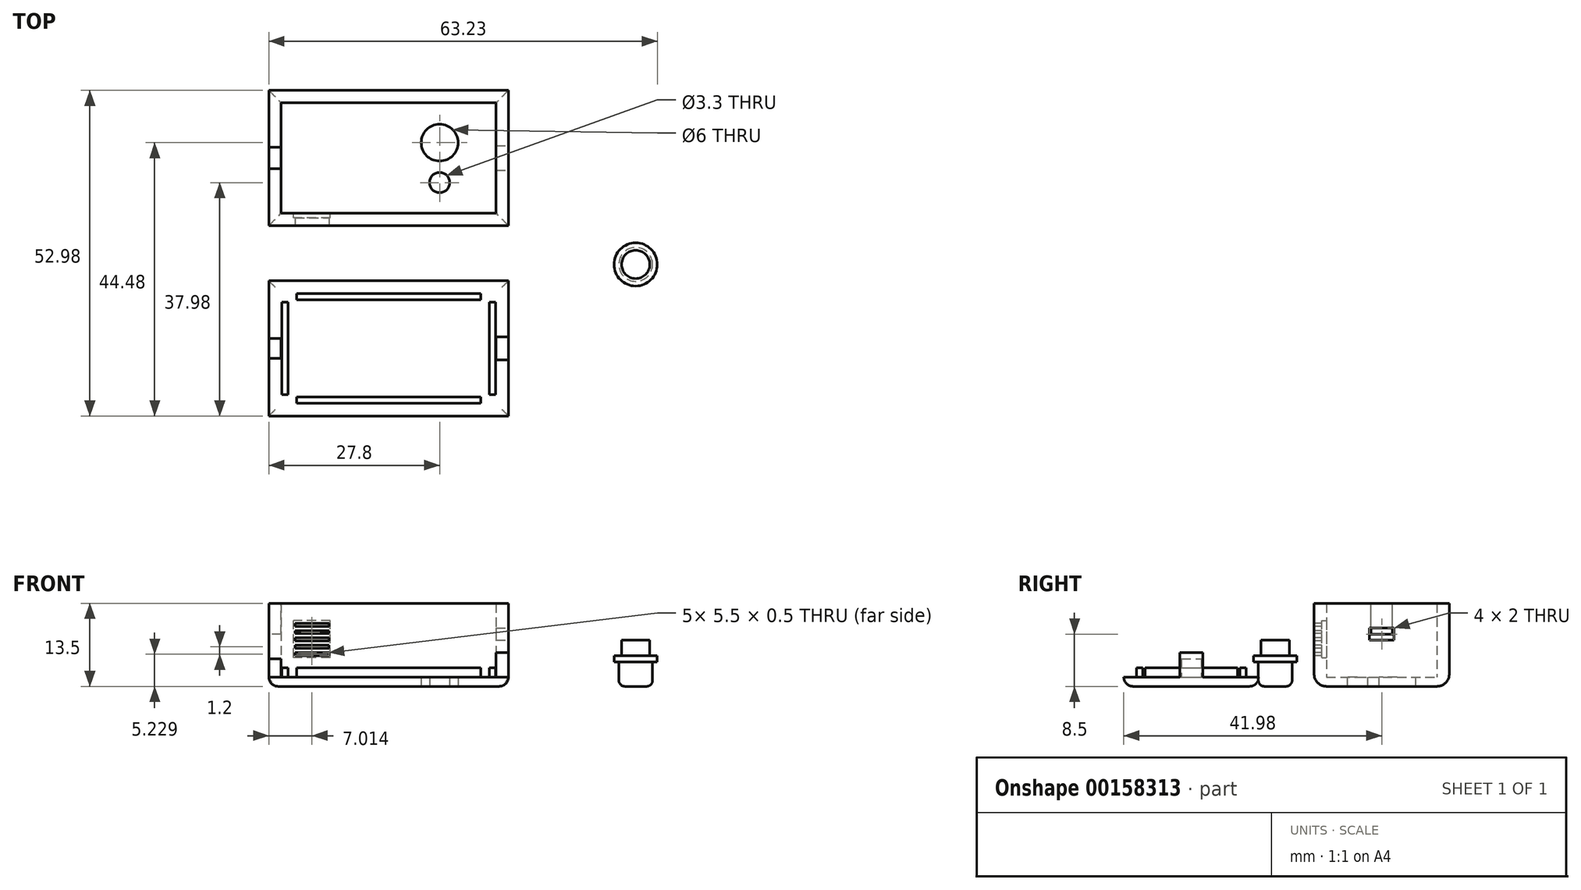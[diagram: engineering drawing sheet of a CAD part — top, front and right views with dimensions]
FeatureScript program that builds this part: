
annotation { "Feature Type Name" : "Feature", "Feature Type Description" : "" }
export const myFeature = defineFeature(function(context is Context, id is Id, definition is map)
    precondition{}
    {
        {
            var Q0;
            Q0=qCreatedBy(makeId("Top.planeOp"),FACE);
            var sketch = newSketch(context, id + "F0", { "sketchPlane" : qUnion([Q0])});
            skLineSegment(sketch, "E0.bottom", {"start": v(17.5, -9) * mm, "end": v(-17.5, -9) * mm});
            skLineSegment(sketch, "E0.top", {"start": v(17.5, 9) * mm, "end": v(-17.5, 9) * mm});
            skLineSegment(sketch, "E0.left", {"start": v(17.5, -9) * mm, "end": v(17.5, 9) * mm});
            skLineSegment(sketch, "E0.right", {"start": v(-17.5, -9) * mm, "end": v(-17.5, 9) * mm});
            skPoint(sketch, "E0.middle", {"position": v(0, 0) * mm});
            skLineSegment(sketch, "E1.0", {"start": v(19.5, 11) * mm, "end": v(-19.5, 11) * mm});
            skLineSegment(sketch, "E1.1", {"start": v(19.5, -11) * mm, "end": v(19.5, 11) * mm});
            skLineSegment(sketch, "E1.2", {"start": v(19.5, -11) * mm, "end": v(-19.5, -11) * mm});
            skLineSegment(sketch, "E1.3", {"start": v(-19.5, -11) * mm, "end": v(-19.5, 11) * mm});
            skPoint(sketch, "E2", {"position": v(8.3, -4) * mm});
            skPoint(sketch, "E3", {"position": v(8.3, 2.5) * mm});
            skSolve(sketch);
        }
        {
            var Q0;
            Q0=makeQuery(id+"F0.imprint","IMPRINT",FACE,{"disambiguationData":[TD([[makeQuery(id+"F0.imprint","IMPRINT",EDGE,{"derivedFrom":sQuery(id+"F0.wireOp",EDGE,"E0.bottom")}),-1.0]])]});
            extrude(context, id + "F1", {"entities" : qUnion([Q0]), "depth" : 1.5 * mm});
        }
        {
            var Q0;
            Q0=makeQuery(id+"F0.imprint","IMPRINT",FACE,{"disambiguationData":[TD([[makeQuery(id+"F0.imprint","IMPRINT",EDGE,{"derivedFrom":sQuery(id+"F0.wireOp",EDGE,"E0.bottom")}),1.0]])]});
            extrude(context, id + "F2", {"entities" : qUnion([Q0]), "operationType" : NewBodyOperationType.ADD, "depth" : 13.5 * mm});
        }
        {
            var Q0;
            Q0=sQuery(id+"F0.wireOp",VERTEX,"E2");
            var Q1;
            Q1=makeQuery(id+"F1.opExtrude","SWEPT_BODY",BODY,{"disambiguationData":[OSD([sQuery(id+"F0.wireOp",EDGE,"E0.bottom"),sQuery(id+"F0.wireOp",EDGE,"E0.top"),sQuery(id+"F0.wireOp",EDGE,"E0.left"),sQuery(id+"F0.wireOp",EDGE,"E0.right")])]});
            hole(context, id + "F3", {"style" : HoleStyle.SIMPLE, "endStyle" : HoleEndStyle.BLIND, "oppositeDirection" : true, "holeDiameter" : 3.3 * mm, "holeDepth" : 5 * mm, "locations" : qUnion([Q0]), "scope" : qUnion([Q1])});
        }
        {
            var Q0;
            Q0=makeQuery(id+"F2.opExtrude","SWEPT_FACE",FACE,{"disambiguationData":[OSD([sQuery(id+"F0.wireOp",EDGE,"E1.2")])]});
            cPlane(context, id + "F4", {"entities" : qUnion([Q0]), "cplaneType" : CPlaneType.OFFSET, "offset" : 2 * mm, "oppositeDirection" : true, "width" : 150 * mm, "height" : 150 * mm});
        }
        {
            var Q0;
            Q0=sQuery(id+"F0.wireOp",VERTEX,"E3");
            var Q1;
            Q1=makeQuery(id+"F1.opExtrude","SWEPT_BODY",BODY,{"disambiguationData":[OSD([sQuery(id+"F0.wireOp",EDGE,"E0.bottom"),sQuery(id+"F0.wireOp",EDGE,"E0.top"),sQuery(id+"F0.wireOp",EDGE,"E0.left"),sQuery(id+"F0.wireOp",EDGE,"E0.right")])]});
            hole(context, id + "F5", {"style" : HoleStyle.SIMPLE, "endStyle" : HoleEndStyle.BLIND, "oppositeDirection" : true, "holeDiameter" : 6 * mm, "holeDepth" : 5 * mm, "locations" : qUnion([Q0]), "scope" : qUnion([Q1])});
        }
        {
            var Q0;
            Q0=makeQuery(id+"F2.opExtrude","SWEPT_FACE",FACE,{"disambiguationData":[OSD([sQuery(id+"F0.wireOp",EDGE,"E1.1")])]});
            var sketch = newSketch(context, id + "F6", { "sketchPlane" : qUnion([Q0])});
            skPoint(sketch, "E4", {"position": v(0, 8.5) * mm});
            skPoint(sketch, "E4.positionSnap0", {"position": v(0, 13.5) * mm});
            skLineSegment(sketch, "E5.bottom", {"start": v(2, 7.5) * mm, "end": v(-2, 7.5) * mm});
            skLineSegment(sketch, "E5.top", {"start": v(2, 9.5) * mm, "end": v(-2, 9.5) * mm});
            skLineSegment(sketch, "E5.left", {"start": v(2, 7.5) * mm, "end": v(2, 9.5) * mm});
            skLineSegment(sketch, "E5.right", {"start": v(-2, 7.5) * mm, "end": v(-2, 9.5) * mm});
            skLineSegment(sketch, "E6.bottom", {"start": v(-2, 9.5) * mm, "end": v(2, 9.5) * mm});
            skLineSegment(sketch, "E6.top", {"start": v(-2, 9.5) * mm, "end": v(2, 9.5) * mm});
            skLineSegment(sketch, "E6.left", {"start": v(-2, 9.5) * mm, "end": v(-2, 9.5) * mm});
            skLineSegment(sketch, "E6.right", {"start": v(2, 9.5) * mm, "end": v(2, 9.5) * mm});
            skLineSegment(sketch, "E7.top", {"start": v(-2, 13.5) * mm, "end": v(2, 13.5) * mm});
            skLineSegment(sketch, "E7.left", {"start": v(-2, 9.5) * mm, "end": v(-2, 13.5) * mm});
            skLineSegment(sketch, "E7.right", {"start": v(2, 9.5) * mm, "end": v(2, 13.5) * mm});
            skSolve(sketch);
        }
        {
            var Q0;
            Q0=qCreatedBy(makeId("Top.planeOp"),FACE);
            var sketch = newSketch(context, id + "F7", { "sketchPlane" : qUnion([Q0])});
            skCircle(sketch, "E8", {"center": v(40.21, -17.32) * mm, "radius": 2.75 * mm});
            skCircle(sketch, "E9", {"center": v(40.21, -17.32) * mm, "radius": 2.3 * mm});
            skSolve(sketch);
        }
        {
            var Q0;
            Q0=makeQuery(id+"F7.imprint","IMPRINT",FACE,{"disambiguationData":[TD([[makeQuery(id+"F7.imprint","IMPRINT",EDGE,{"derivedFrom":sQuery(id+"F7.wireOp",EDGE,"E9")}),1.0]])]});
            extrude(context, id + "F8", {"entities" : qUnion([Q0]), "depth" : 7.5 * mm});
        }
        {
            var Q0;
            Q0=makeQuery(id+"F7.imprint","IMPRINT",FACE,{"disambiguationData":[TD([[makeQuery(id+"F7.imprint","IMPRINT",EDGE,{"derivedFrom":sQuery(id+"F7.wireOp",EDGE,"E8")}),1.0]])]});
            extrude(context, id + "F9", {"entities" : qUnion([Q0]), "operationType" : NewBodyOperationType.ADD, "depth" : 4 * mm});
        }
        {
            var Q0;
            {var subQ0=sQuery(id+"F7.wireOp",EDGE,"E9");Q0=makeQuery(id+"F9.boolean.opBoolean","MERGE",FACE,{"derivedFrom":[makeQuery(id+"F8.opExtrude","CAP_FACE",FACE,{"disambiguationData":[OSD([subQ0])],"isStart":true}),makeQuery(id+"F9.opExtrude","CAP_FACE",FACE,{"disambiguationData":[OSD([sQuery(id+"F7.wireOp",EDGE,"E8"),subQ0])],"isStart":true})]});}
            var Q1;
            Q1=makeQuery(id+"F9.opExtrude","CAP_EDGE",EDGE,{"disambiguationData":[OSD([sQuery(id+"F7.wireOp",EDGE,"E8")])],"isStart":true});
            fillet(context, id + "F10", {"entities" : qUnion([Q0, Q1]), "radius" : 1 * mm, "tangentPropagation" : true, "allowEdgeOverflow" : false});
        }
        {
            var Q0;
            Q0=makeQuery(id+"F9.opExtrude","CAP_FACE",FACE,{"disambiguationData":[OSD([sQuery(id+"F7.wireOp",EDGE,"E8"),sQuery(id+"F7.wireOp",EDGE,"E9")])],"isStart":false});
            var sketch = newSketch(context, id + "F11", { "sketchPlane" : qUnion([Q0])});
            skCircle(sketch, "E10", {"center": v(40.21, -17.32) * mm, "radius": 2.75 * mm});
            skPoint(sketch, "E10.first.point", {"position": v(37.94, -15.78) * mm});
            skPoint(sketch, "E10.second.point", {"position": v(37.8, -16.01) * mm});
            skPoint(sketch, "E10.third.point", {"position": v(37.94, -15.78) * mm});
            skCircle(sketch, "E11", {"center": v(40.21, -17.32) * mm, "radius": 3.51 * mm});
            skSolve(sketch);
        }
        {
            var Q0;
            Q0=makeQuery(id+"F11.imprint","IMPRINT",FACE,{"disambiguationData":[TD([[makeQuery(id+"F11.imprint","IMPRINT",EDGE,{"derivedFrom":sQuery(id+"F11.wireOp",EDGE,"E10")}),-1.0]])]});
            var Q1;
            Q1=makeQuery(id+"F11.imprint","IMPRINT",FACE,{"disambiguationData":[TD([[makeQuery(id+"F11.imprint","IMPRINT",EDGE,{"derivedFrom":sQuery(id+"F11.wireOp",EDGE,"E10")}),1.0]])]});
            extrude(context, id + "F12", {"entities" : qUnion([Q0, Q1]), "operationType" : NewBodyOperationType.ADD, "depth" : 1 * mm});
        }
        {
            var Q0;
            Q0=makeQuery(id+"F2.opExtrude","CAP_FACE",FACE,{"disambiguationData":[OSD([sQuery(id+"F0.wireOp",EDGE,"E0.bottom"),sQuery(id+"F0.wireOp",EDGE,"E0.top"),sQuery(id+"F0.wireOp",EDGE,"E0.left"),sQuery(id+"F0.wireOp",EDGE,"E0.right"),sQuery(id+"F0.wireOp",EDGE,"E1.0"),sQuery(id+"F0.wireOp",EDGE,"E1.1"),sQuery(id+"F0.wireOp",EDGE,"E1.2"),sQuery(id+"F0.wireOp",EDGE,"E1.3")])],"isStart":false});
            var sketch = newSketch(context, id + "F13", { "sketchPlane" : qUnion([Q0])});
            skLineSegment(sketch, "E12.bottom", {"start": v(-19.5, 11) * mm, "end": v(19.5, 11) * mm});
            skLineSegment(sketch, "E12.top", {"start": v(-19.5, -11) * mm, "end": v(19.5, -11) * mm});
            skLineSegment(sketch, "E12.left", {"start": v(-19.5, 11) * mm, "end": v(-19.5, -11) * mm});
            skLineSegment(sketch, "E12.right", {"start": v(19.5, 11) * mm, "end": v(19.5, -11) * mm});
            skSolve(sketch);
        }
        {
            var Q0;
            Q0=qCreatedBy(id+"F4.planeOp",FACE);
            var sketch = newSketch(context, id + "F14", { "sketchPlane" : qUnion([Q0])});
            skPoint(sketch, "E13", {"position": v(-12.5, 7.7) * mm});
            skLineSegment(sketch, "E14.bottom", {"start": v(-9.5, 4.7) * mm, "end": v(-15.5, 4.7) * mm});
            skLineSegment(sketch, "E14.top", {"start": v(-9.5, 10.7) * mm, "end": v(-15.5, 10.7) * mm});
            skLineSegment(sketch, "E14.left", {"start": v(-9.5, 4.7) * mm, "end": v(-9.5, 10.7) * mm});
            skLineSegment(sketch, "E14.right", {"start": v(-15.5, 4.7) * mm, "end": v(-15.5, 10.7) * mm});
            skSolve(sketch);
        }
        {
            var Q0;
            Q0=makeQuery(id+"F14.imprint","IMPRINT",FACE,{"disambiguationData":[TD([[makeQuery(id+"F14.imprint","IMPRINT",EDGE,{"derivedFrom":sQuery(id+"F14.wireOp",EDGE,"E14.bottom")}),-1.0]])]});
            extrude(context, id + "F15", {"entities" : qUnion([Q0]), "operationType" : NewBodyOperationType.REMOVE, "endBound" : BoundingType.SYMMETRIC, "depth" : 1.5 * mm});
        }
        {
            var Q0;
            Q0=makeQuery(id+"F2.opExtrude","SWEPT_FACE",FACE,{"disambiguationData":[OSD([sQuery(id+"F0.wireOp",EDGE,"E1.3")])]});
            var sketch = newSketch(context, id + "F16", { "sketchPlane" : qUnion([Q0])});
            skPoint(sketch, "E15", {"position": v(0, 11) * mm});
            skPoint(sketch, "E15.positionSnap0", {"position": v(0, 13.5) * mm});
            skLineSegment(sketch, "E16.bottom", {"start": v(1.75, 8.5) * mm, "end": v(-1.75, 8.5) * mm});
            skLineSegment(sketch, "E16.top", {"start": v(1.75, 13.5) * mm, "end": v(-1.75, 13.5) * mm});
            skLineSegment(sketch, "E16.left", {"start": v(1.75, 8.5) * mm, "end": v(1.75, 13.5) * mm});
            skLineSegment(sketch, "E16.right", {"start": v(-1.75, 8.5) * mm, "end": v(-1.75, 13.5) * mm});
            skSolve(sketch);
        }
        {
            var Q0;
            Q0=makeQuery(id+"F16.imprint","IMPRINT",FACE,{"disambiguationData":[TD([[makeQuery(id+"F16.imprint","IMPRINT",EDGE,{"derivedFrom":sQuery(id+"F16.wireOp",EDGE,"E16.bottom")}),-1.0]])]});
            extrude(context, id + "F17", {"entities" : qUnion([Q0]), "operationType" : NewBodyOperationType.REMOVE, "oppositeDirection" : true, "depth" : 5 * mm});
        }
        {
            var Q0;
            Q0=qCreatedBy(makeId("Top.planeOp"),FACE);
            var sketch = newSketch(context, id + "F18", { "sketchPlane" : qUnion([Q0])});
            skLineSegment(sketch, "E17.bottom", {"start": v(19.5, -41.98) * mm, "end": v(-19.5, -41.98) * mm});
            skLineSegment(sketch, "E17.top", {"start": v(19.5, -19.98) * mm, "end": v(-19.5, -19.98) * mm});
            skLineSegment(sketch, "E17.left", {"start": v(19.5, -41.98) * mm, "end": v(19.5, -19.98) * mm});
            skLineSegment(sketch, "E17.right", {"start": v(-19.5, -41.98) * mm, "end": v(-19.5, -19.98) * mm});
            skPoint(sketch, "E17.middle", {"position": v(0, -30.98) * mm});
            skLineSegment(sketch, "E18.bottom", {"start": v(15, -39.88) * mm, "end": v(-15, -39.88) * mm});
            skLineSegment(sketch, "E18.top", {"start": v(15, -38.88) * mm, "end": v(-15, -38.88) * mm});
            skLineSegment(sketch, "E18.left", {"start": v(15, -39.88) * mm, "end": v(15, -38.88) * mm});
            skLineSegment(sketch, "E18.right", {"start": v(-15, -39.88) * mm, "end": v(-15, -38.88) * mm});
            skPoint(sketch, "E18.middle", {"position": v(0, -39.38) * mm});
            skPoint(sketch, "E18.middle.positionSnap0", {"position": v(0, -41.98) * mm});
            skPoint(sketch, "E18.centerSnap0", {"position": v(0, -41.98) * mm});
            skLineSegment(sketch, "E19.bottom", {"start": v(15, -23.1) * mm, "end": v(-15, -23.1) * mm});
            skLineSegment(sketch, "E19.top", {"start": v(15, -22.1) * mm, "end": v(-15, -22.1) * mm});
            skLineSegment(sketch, "E19.left", {"start": v(15, -23.1) * mm, "end": v(15, -22.1) * mm});
            skLineSegment(sketch, "E19.right", {"start": v(-15, -23.1) * mm, "end": v(-15, -22.1) * mm});
            skPoint(sketch, "E19.middle", {"position": v(0, -22.6) * mm});
            skLineSegment(sketch, "E20.bottom", {"start": v(-16.4, -38.48) * mm, "end": v(-17.4, -38.48) * mm});
            skLineSegment(sketch, "E20.top", {"start": v(-16.4, -23.48) * mm, "end": v(-17.4, -23.48) * mm});
            skLineSegment(sketch, "E20.left", {"start": v(-16.4, -38.48) * mm, "end": v(-16.4, -23.48) * mm});
            skLineSegment(sketch, "E20.right", {"start": v(-17.4, -38.48) * mm, "end": v(-17.4, -23.48) * mm});
            skPoint(sketch, "E20.middle", {"position": v(-16.9, -30.98) * mm});
            skPoint(sketch, "E20.middle.positionSnap0", {"position": v(-19.5, -30.98) * mm});
            skPoint(sketch, "E20.centerSnap0", {"position": v(-19.5, -30.98) * mm});
            skLineSegment(sketch, "E21.bottom", {"start": v(17.4, -38.48) * mm, "end": v(16.4, -38.48) * mm});
            skLineSegment(sketch, "E21.top", {"start": v(17.4, -23.48) * mm, "end": v(16.4, -23.48) * mm});
            skLineSegment(sketch, "E21.left", {"start": v(17.4, -38.48) * mm, "end": v(17.4, -23.48) * mm});
            skLineSegment(sketch, "E21.right", {"start": v(16.4, -38.48) * mm, "end": v(16.4, -23.48) * mm});
            skPoint(sketch, "E21.middle", {"position": v(16.9, -30.98) * mm});
            skPoint(sketch, "E21.middle.positionSnap0", {"position": v(19.5, -30.98) * mm});
            skPoint(sketch, "E21.centerSnap0", {"position": v(19.5, -30.98) * mm});
            skLineSegment(sketch, "E22.bottom", {"start": v(-17.5, -32.58) * mm, "end": v(-19.5, -32.58) * mm});
            skLineSegment(sketch, "E22.top", {"start": v(-17.5, -29.38) * mm, "end": v(-19.5, -29.38) * mm});
            skLineSegment(sketch, "E22.left", {"start": v(-17.5, -32.58) * mm, "end": v(-17.5, -29.38) * mm});
            skLineSegment(sketch, "E22.right", {"start": v(-19.5, -32.58) * mm, "end": v(-19.5, -29.38) * mm});
            skPoint(sketch, "E22.middle", {"position": v(-18.5, -30.98) * mm});
            skLineSegment(sketch, "E23.bottom", {"start": v(19.5, -32.83) * mm, "end": v(17.5, -32.83) * mm});
            skLineSegment(sketch, "E23.top", {"start": v(19.5, -29.13) * mm, "end": v(17.5, -29.13) * mm});
            skLineSegment(sketch, "E23.left", {"start": v(19.5, -32.83) * mm, "end": v(19.5, -29.13) * mm});
            skLineSegment(sketch, "E23.right", {"start": v(17.5, -32.83) * mm, "end": v(17.5, -29.13) * mm});
            skPoint(sketch, "E23.middle", {"position": v(18.5, -30.98) * mm});
            skSolve(sketch);
        }
        {
            var Q0;
            {var subQ1=sQuery(id+"F18.wireOp",EDGE,"E17.bottom");Q0=makeQuery(id+"F18.imprint","IMPRINT",FACE,{"disambiguationData":[TD([[makeQuery(id+"F18.imprint","IMPRINT",EDGE,{"derivedFrom":subQ1}),-1.0]])]});}
            extrude(context, id + "F19", {"entities" : qUnion([Q0]), "depth" : 1.5 * mm});
        }
        {
            var Q0;
            Q0=makeQuery(id+"F18.imprint","IMPRINT",FACE,{"disambiguationData":[TD([[makeQuery(id+"F18.imprint","IMPRINT",EDGE,{"derivedFrom":sQuery(id+"F18.wireOp",EDGE,"E19.bottom")}),-1.0]])]});
            var Q1;
            Q1=makeQuery(id+"F18.imprint","IMPRINT",FACE,{"disambiguationData":[TD([[makeQuery(id+"F18.imprint","IMPRINT",EDGE,{"derivedFrom":sQuery(id+"F18.wireOp",EDGE,"E20.bottom")}),-1.0]])]});
            var Q2;
            Q2=makeQuery(id+"F18.imprint","IMPRINT",FACE,{"disambiguationData":[TD([[makeQuery(id+"F18.imprint","IMPRINT",EDGE,{"derivedFrom":sQuery(id+"F18.wireOp",EDGE,"E18.bottom")}),-1.0]])]});
            var Q3;
            Q3=makeQuery(id+"F18.imprint","IMPRINT",FACE,{"disambiguationData":[TD([[makeQuery(id+"F18.imprint","IMPRINT",EDGE,{"derivedFrom":sQuery(id+"F18.wireOp",EDGE,"E21.bottom")}),-1.0]])]});
            extrude(context, id + "F20", {"entities" : qUnion([Q0, Q1, Q2, Q3]), "operationType" : NewBodyOperationType.ADD, "depth" : 3 * mm});
        }
        {
            var Q0;
            Q0=makeQuery(id+"F6.imprint","IMPRINT",FACE,{"disambiguationData":[TD([[makeQuery(id+"F6.imprint","IMPRINT",EDGE,{"derivedFrom":sQuery(id+"F6.wireOp",EDGE,"E5.bottom")}),-1.0]])]});
            var Q1;
            Q1=makeQuery(id+"F6.imprint","IMPRINT",FACE,{"disambiguationData":[TD([[makeQuery(id+"F6.imprint","IMPRINT",EDGE,{"derivedFrom":sQuery(id+"F6.wireOp",EDGE,"E6.bottom")}),1.0]])]});
            extrude(context, id + "F21", {"entities" : qUnion([Q0, Q1]), "operationType" : NewBodyOperationType.REMOVE, "oppositeDirection" : true, "depth" : 5 * mm});
        }
        {
            var Q0;
            {var subQ2=sQuery(id+"F18.wireOp",EDGE,"E23.bottom");Q0=makeQuery(id+"F18.imprint","IMPRINT",FACE,{"disambiguationData":[TD([[makeQuery(id+"F18.imprint","IMPRINT",EDGE,{"derivedFrom":subQ2}),-1.0]])]});}
            extrude(context, id + "F22", {"entities" : qUnion([Q0]), "operationType" : NewBodyOperationType.ADD, "depth" : 5.5 * mm});
        }
        {
            var Q0;
            Q0=makeQuery(id+"F2.opExtrude","SWEPT_FACE",FACE,{"disambiguationData":[OSD([sQuery(id+"F0.wireOp",EDGE,"E1.2")])]});
            var sketch = newSketch(context, id + "F23", { "sketchPlane" : qUnion([Q0])});
            skLineSegment(sketch, "E24.bottom", {"start": v(-15.24, 4.98) * mm, "end": v(-15.24, 5.48) * mm});
            skLineSegment(sketch, "E24.top", {"start": v(-9.74, 4.98) * mm, "end": v(-9.74, 5.48) * mm});
            skLineSegment(sketch, "E24.left", {"start": v(-15.24, 4.98) * mm, "end": v(-9.74, 4.98) * mm});
            skLineSegment(sketch, "E24.right", {"start": v(-15.24, 5.48) * mm, "end": v(-9.74, 5.48) * mm});
            skLineSegment(sketch, "E25.1.0.0", {"start": v(-15.24, 6.68) * mm, "end": v(-9.74, 6.68) * mm});
            skLineSegment(sketch, "E25.1.0.1", {"start": v(-15.24, 6.18) * mm, "end": v(-9.74, 6.18) * mm});
            skLineSegment(sketch, "E25.1.0.2", {"start": v(-9.74, 6.18) * mm, "end": v(-9.74, 6.68) * mm});
            skLineSegment(sketch, "E25.1.0.3", {"start": v(-15.24, 6.18) * mm, "end": v(-15.24, 6.68) * mm});
            skLineSegment(sketch, "E25.2.0.0", {"start": v(-15.24, 7.88) * mm, "end": v(-9.74, 7.88) * mm});
            skLineSegment(sketch, "E25.2.0.1", {"start": v(-15.24, 7.38) * mm, "end": v(-9.74, 7.38) * mm});
            skLineSegment(sketch, "E25.2.0.2", {"start": v(-9.74, 7.38) * mm, "end": v(-9.74, 7.88) * mm});
            skLineSegment(sketch, "E25.2.0.3", {"start": v(-15.24, 7.38) * mm, "end": v(-15.24, 7.88) * mm});
            skLineSegment(sketch, "E25.3.0.0", {"start": v(-15.24, 9.08) * mm, "end": v(-9.74, 9.08) * mm});
            skLineSegment(sketch, "E25.3.0.1", {"start": v(-15.24, 8.58) * mm, "end": v(-9.74, 8.58) * mm});
            skLineSegment(sketch, "E25.3.0.2", {"start": v(-9.74, 8.58) * mm, "end": v(-9.74, 9.08) * mm});
            skLineSegment(sketch, "E25.3.0.3", {"start": v(-15.24, 8.58) * mm, "end": v(-15.24, 9.08) * mm});
            skLineSegment(sketch, "E25.4.0.0", {"start": v(-15.24, 10.28) * mm, "end": v(-9.74, 10.28) * mm});
            skLineSegment(sketch, "E25.4.0.1", {"start": v(-15.24, 9.78) * mm, "end": v(-9.74, 9.78) * mm});
            skLineSegment(sketch, "E25.4.0.2", {"start": v(-9.74, 9.78) * mm, "end": v(-9.74, 10.28) * mm});
            skLineSegment(sketch, "E25.4.0.3", {"start": v(-15.24, 9.78) * mm, "end": v(-15.24, 10.28) * mm});
            skLineSegment(sketch, "E25.direction1", {"start": v(-9.74, 4.98) * mm, "end": v(-9.74, 6.18) * mm, "construction": true});
            skSolve(sketch);
        }
        {
            var Q0;
            Q0=makeQuery(id+"F23.imprint","IMPRINT",FACE,{"disambiguationData":[TD([[makeQuery(id+"F23.imprint","IMPRINT",EDGE,{"derivedFrom":sQuery(id+"F23.wireOp",EDGE,"E24.bottom")}),-1.0]])]});
            var Q1;
            Q1=makeQuery(id+"F23.imprint","IMPRINT",FACE,{"disambiguationData":[TD([[makeQuery(id+"F23.imprint","IMPRINT",EDGE,{"derivedFrom":sQuery(id+"F23.wireOp",EDGE,"E25.1.0.0")}),-1.0]])]});
            var Q2;
            Q2=makeQuery(id+"F23.imprint","IMPRINT",FACE,{"disambiguationData":[TD([[makeQuery(id+"F23.imprint","IMPRINT",EDGE,{"derivedFrom":sQuery(id+"F23.wireOp",EDGE,"E25.2.0.0")}),-1.0]])]});
            var Q3;
            Q3=makeQuery(id+"F23.imprint","IMPRINT",FACE,{"disambiguationData":[TD([[makeQuery(id+"F23.imprint","IMPRINT",EDGE,{"derivedFrom":sQuery(id+"F23.wireOp",EDGE,"E25.3.0.0")}),-1.0]])]});
            var Q4;
            Q4=makeQuery(id+"F23.imprint","IMPRINT",FACE,{"disambiguationData":[TD([[makeQuery(id+"F23.imprint","IMPRINT",EDGE,{"derivedFrom":sQuery(id+"F23.wireOp",EDGE,"E25.4.0.0")}),-1.0]])]});
            var Q5;
            Q5=makeQuery(id+"F23.imprint","IMPRINT",FACE,{"disambiguationData":[TD([[makeQuery(id+"F23.imprint","IMPRINT",EDGE,{"derivedFrom":sQuery(id+"F23.wireOp",EDGE,"61a891a3-ae5f-4639-807f-27233e564d6f.0.5.0")}),-1.0]])]});
            extrude(context, id + "F24", {"entities" : qUnion([Q0, Q1, Q2, Q3, Q4, Q5]), "operationType" : NewBodyOperationType.REMOVE, "oppositeDirection" : true, "depth" : 5 * mm});
        }
        {
            var Q0;
            {var subQ2=sQuery(id+"F18.wireOp",EDGE,"E22.bottom");Q0=makeQuery(id+"F18.imprint","IMPRINT",FACE,{"disambiguationData":[TD([[makeQuery(id+"F18.imprint","IMPRINT",EDGE,{"derivedFrom":subQ2}),-1.0]])]});}
            extrude(context, id + "F25", {"entities" : qUnion([Q0]), "operationType" : NewBodyOperationType.ADD, "depth" : 4.5 * mm});
        }
        {
            var Q0;
            Q0=makeQuery(id+"F2.opExtrude","CAP_EDGE",EDGE,{"disambiguationData":[OSD([sQuery(id+"F0.wireOp",EDGE,"E1.2")])],"isStart":true});
            var Q1;
            Q1=makeQuery(id+"F2.opExtrude","CAP_EDGE",EDGE,{"disambiguationData":[OSD([sQuery(id+"F0.wireOp",EDGE,"E1.3")])],"isStart":true});
            var Q2;
            Q2=makeQuery(id+"F2.opExtrude","CAP_EDGE",EDGE,{"disambiguationData":[OSD([sQuery(id+"F0.wireOp",EDGE,"E1.1")])],"isStart":true});
            var Q3;
            Q3=makeQuery(id+"F2.opExtrude","CAP_EDGE",EDGE,{"disambiguationData":[OSD([sQuery(id+"F0.wireOp",EDGE,"E1.0")])],"isStart":true});
            fillet(context, id + "F26", {"entities" : qUnion([Q0, Q1, Q2, Q3]), "radius" : 2 * mm, "tangentPropagation" : true, "allowEdgeOverflow" : false});
        }
        {
            var Q0;
            {var subQ0=sQuery(id+"F18.wireOp",EDGE,"E22.left");var subQ1=sQuery(id+"F18.wireOp",EDGE,"E22.top");var subQ2=sQuery(id+"F18.wireOp",EDGE,"E22.bottom");var subQ3=sQuery(id+"F18.wireOp",EDGE,"E17.right");var subQ4=sQuery(id+"F18.wireOp",EDGE,"E23.right");var subQ5=sQuery(id+"F18.wireOp",EDGE,"E23.top");var subQ6=sQuery(id+"F18.wireOp",EDGE,"E23.bottom");var subQ7=sQuery(id+"F18.wireOp",EDGE,"E17.left");var subQ8=sQuery(id+"F18.wireOp",EDGE,"E21.right");var subQ9=sQuery(id+"F18.wireOp",EDGE,"E21.left");var subQ10=sQuery(id+"F18.wireOp",EDGE,"E21.top");var subQ11=sQuery(id+"F18.wireOp",EDGE,"E21.bottom");var subQ12=sQuery(id+"F18.wireOp",EDGE,"E20.right");var subQ13=sQuery(id+"F18.wireOp",EDGE,"E20.left");var subQ14=sQuery(id+"F18.wireOp",EDGE,"E20.top");var subQ15=sQuery(id+"F18.wireOp",EDGE,"E20.bottom");var subQ16=sQuery(id+"F18.wireOp",EDGE,"E19.right");var subQ17=sQuery(id+"F18.wireOp",EDGE,"E19.left");var subQ18=sQuery(id+"F18.wireOp",EDGE,"E19.top");var subQ19=sQuery(id+"F18.wireOp",EDGE,"E19.bottom");var subQ20=sQuery(id+"F18.wireOp",EDGE,"E18.right");var subQ21=sQuery(id+"F18.wireOp",EDGE,"E18.left");var subQ22=sQuery(id+"F18.wireOp",EDGE,"E18.top");var subQ23=sQuery(id+"F18.wireOp",EDGE,"E18.bottom");Q0=makeQuery(id+"F25.boolean.opBoolean","MERGE",FACE,{"derivedFrom":[makeQuery(id+"F22.boolean.opBoolean","MERGE",FACE,{"derivedFrom":[makeQuery(id+"F20.boolean.opBoolean","MERGE",FACE,{"derivedFrom":[makeQuery(id+"F19.opExtrude","CAP_FACE",FACE,{"disambiguationData":[OSD([sQuery(id+"F18.wireOp",EDGE,"E17.bottom"),sQuery(id+"F18.wireOp",EDGE,"E17.top"),subQ7,subQ3,subQ23,subQ22,subQ21,subQ20,subQ19,subQ18,subQ17,subQ16,subQ15,subQ14,subQ13,subQ12,subQ11,subQ10,subQ9,subQ8,subQ2,subQ1,subQ0,subQ6,subQ5,subQ4])],"isStart":true}),makeQuery(id+"F20.opExtrude","CAP_FACE",FACE,{"disambiguationData":[OSD([subQ23,subQ22,subQ21,subQ20])],"isStart":true}),makeQuery(id+"F20.opExtrude","CAP_FACE",FACE,{"disambiguationData":[OSD([subQ19,subQ18,subQ17,subQ16])],"isStart":true}),makeQuery(id+"F20.opExtrude","CAP_FACE",FACE,{"disambiguationData":[OSD([subQ15,subQ14,subQ13,subQ12])],"isStart":true}),makeQuery(id+"F20.opExtrude","CAP_FACE",FACE,{"disambiguationData":[OSD([subQ11,subQ10,subQ9,subQ8])],"isStart":true})]}),makeQuery(id+"F22.opExtrude","CAP_FACE",FACE,{"disambiguationData":[OSD([subQ7,subQ6,subQ5,subQ4])],"isStart":true})]}),makeQuery(id+"F25.opExtrude","CAP_FACE",FACE,{"disambiguationData":[OSD([subQ3,subQ2,subQ1,subQ0])],"isStart":true})]});}
            fillet(context, id + "F27", {"entities" : qUnion([Q0]), "radius" : 1.5 * mm, "tangentPropagation" : true, "allowEdgeOverflow" : false});
        }
    });
